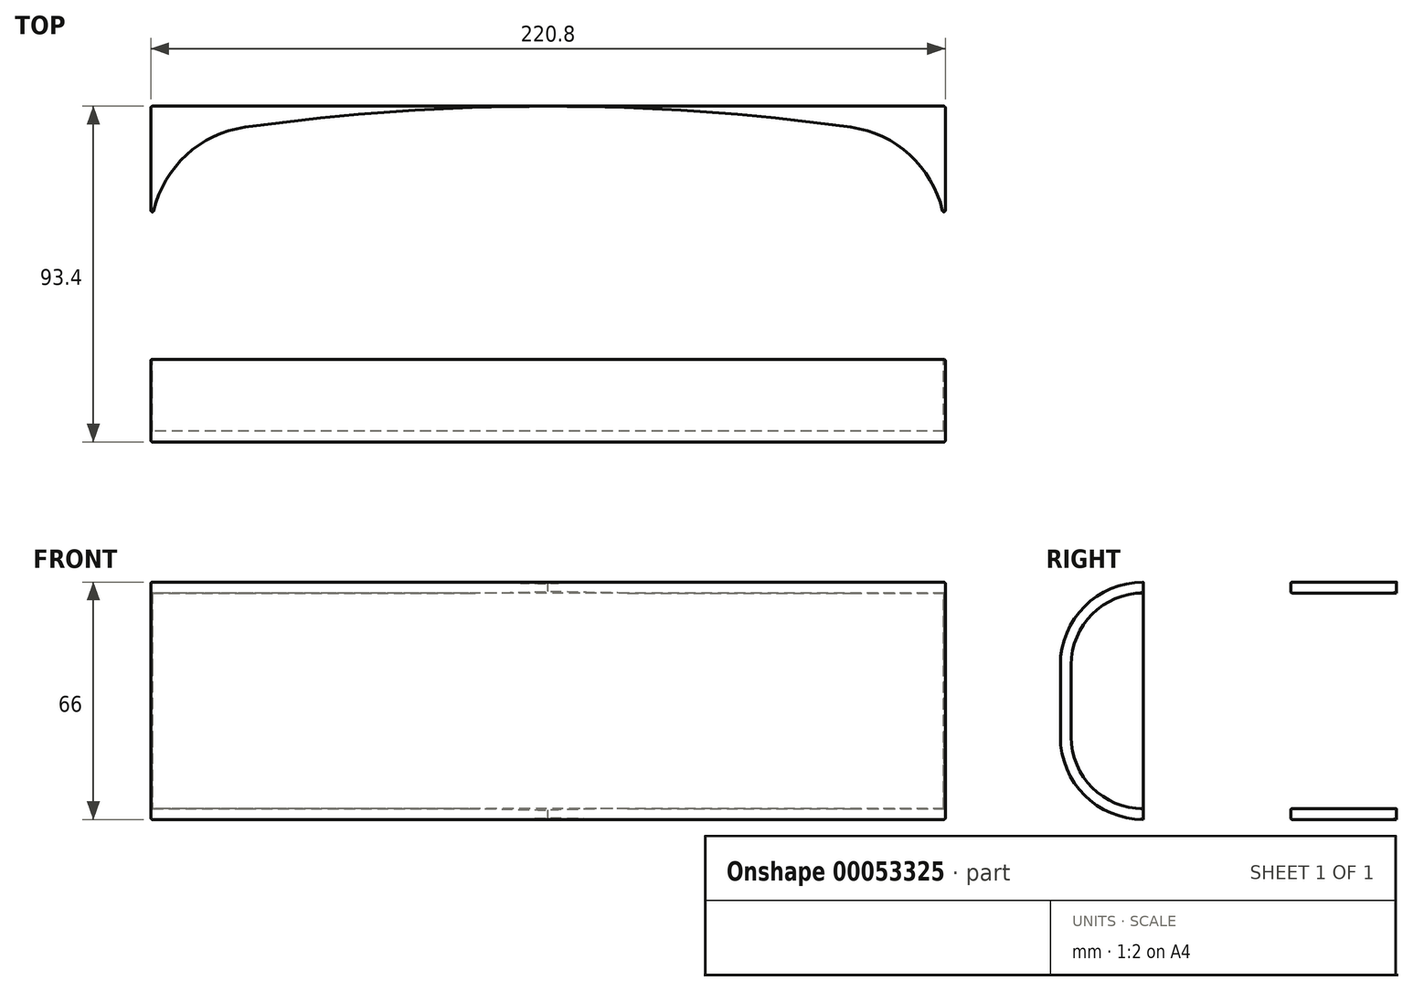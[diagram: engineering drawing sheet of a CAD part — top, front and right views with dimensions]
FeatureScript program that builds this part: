
annotation { "Feature Type Name" : "Feature", "Feature Type Description" : "" }
export const myFeature = defineFeature(function(context is Context, id is Id, definition is map)
    precondition{}
    {
        {
            var Q0;
            Q0=qCreatedBy(makeId("Top.planeOp"),FACE);
            var sketch = newSketch(context, id + "F0", { "sketchPlane" : qUnion([Q0])});
            skLineSegment(sketch, "E0.rect.bottom", {"start": v(110, 40) * mm, "end": v(-110, 40) * mm});
            skLineSegment(sketch, "E0.rect.top", {"start": v(110, -40) * mm, "end": v(-110, -40) * mm});
            skLineSegment(sketch, "E0.rect.left", {"start": v(110, 40) * mm, "end": v(110, -40) * mm});
            skLineSegment(sketch, "E0.rect.right", {"start": v(-110, 40) * mm, "end": v(-110, -40) * mm});
            skPoint(sketch, "E0.rect.middle", {"position": v(0, 0) * mm});
            skArc(sketch, "E1", {"start": v(110, 40) * mm, "mid": v(0, 50) * mm, "end": v(-110, 40) * mm});
            skSolve(sketch);
        }
        {
            var Q0;
            Q0=makeQuery(id+"F0.imprint","IMPRINT",FACE,{"disambiguationData":[TD([[makeQuery(id+"F0.imprint","IMPRINT",EDGE,{"derivedFrom":sQuery(id+"F0.wireOp",EDGE,"E0.rect.bottom")}),1.0]])]});
            var Q1;
            Q1=makeQuery(id+"F0.imprint","IMPRINT",FACE,{"disambiguationData":[TD([[makeQuery(id+"F0.imprint","IMPRINT",EDGE,{"derivedFrom":sQuery(id+"F0.wireOp",EDGE,"E0.rect.bottom")}),-1.0]])]});
            extrude(context, id + "F1", {"entities" : qUnion([Q0, Q1]), "depth" : 60 * mm});
        }
        {
            var Q0;
            Q0=makeQuery(id+"F1.opExtrude","SWEPT_EDGE",EDGE,{"disambiguationData":[OSD([sQuery(id+"F0.wireOp",EDGE,"E0.rect.bottom"),sQuery(id+"F0.wireOp",EDGE,"E0.rect.right"),sQuery(id+"F0.wireOp",EDGE,"E1")])]});
            var Q1;
            Q1=makeQuery(id+"F1.opExtrude","SWEPT_EDGE",EDGE,{"disambiguationData":[OSD([sQuery(id+"F0.wireOp",EDGE,"E0.rect.bottom"),sQuery(id+"F0.wireOp",EDGE,"E0.rect.left"),sQuery(id+"F0.wireOp",EDGE,"E1")])]});
            fillet(context, id + "F2", {"entities" : qUnion([Q0, Q1]), "radius" : 30 * mm, "tangentPropagation" : true, "allowEdgeOverflow" : false});
        }
        {
            var Q0;
            Q0=makeQuery(id+"F1.opExtrude","CAP_EDGE",EDGE,{"disambiguationData":[OSD([sQuery(id+"F0.wireOp",EDGE,"E0.rect.top")])],"isStart":false});
            var Q1;
            Q1=makeQuery(id+"F1.opExtrude","CAP_EDGE",EDGE,{"disambiguationData":[OSD([sQuery(id+"F0.wireOp",EDGE,"E0.rect.top")])],"isStart":true});
            fillet(context, id + "F3", {"entities" : qUnion([Q0, Q1]), "radius" : 20 * mm, "tangentPropagation" : true, "allowEdgeOverflow" : false});
        }
        {
            var Q0;
            Q0=makeQuery(id+"F1.opExtrude","SWEPT_FACE",FACE,{"disambiguationData":[OSD([sQuery(id+"F0.wireOp",EDGE,"E0.rect.left")])]});
            var sketch = newSketch(context, id + "F4", { "sketchPlane" : qUnion([Q0])});
            skLineSegment(sketch, "E2.0", {"start": v(14.46, -3) * mm, "end": v(-20, -3) * mm});
            skLineSegment(sketch, "E2.1", {"start": v(14.46, 63) * mm, "end": v(-20, 63) * mm});
            skArc(sketch, "E2.2", {"start": v(-20, 63) * mm, "mid": v(-36.26, 56.26) * mm, "end": v(-43, 40) * mm});
            skLineSegment(sketch, "E2.3", {"start": v(-43, 40) * mm, "end": v(-43, 20) * mm});
            skArc(sketch, "E2.4", {"start": v(-43, 20) * mm, "mid": v(-36.26, 3.74) * mm, "end": v(-20, -3) * mm});
            skLineSegment(sketch, "E3", {"start": v(14.46, 63) * mm, "end": v(50.4, 63) * mm});
            skLineSegment(sketch, "E4.0.0", {"start": v(50, 60) * mm, "end": v(44.17, 60) * mm});
            skLineSegment(sketch, "E4.0.1", {"start": v(44.17, 60) * mm, "end": v(44.17, 0) * mm});
            skLineSegment(sketch, "E4.0.2", {"start": v(44.17, 0) * mm, "end": v(50, 0) * mm});
            skLineSegment(sketch, "E4.0.3", {"start": v(44.17, 0) * mm, "end": v(44.17, 60) * mm});
            skLineSegment(sketch, "E5", {"start": v(14.46, -3) * mm, "end": v(50.4, -3) * mm});
            skLineSegment(sketch, "E6", {"start": v(50.4, -3) * mm, "end": v(50.4, 0) * mm});
            skLineSegment(sketch, "E7", {"start": v(50.4, 0) * mm, "end": v(50, 0) * mm});
            skLineSegment(sketch, "E8", {"start": v(50, 60) * mm, "end": v(50.4, 60) * mm});
            skLineSegment(sketch, "E9", {"start": v(50.4, 60) * mm, "end": v(50.4, 63) * mm});
            skLineSegment(sketch, "E10.0", {"start": v(14.46, 60) * mm, "end": v(44.17, 60) * mm});
            skLineSegment(sketch, "E11.0", {"start": v(14.46, 60) * mm, "end": v(-20, 60) * mm});
            skArc(sketch, "E12.0", {"start": v(-20, 60) * mm, "mid": v(-34.14, 54.14) * mm, "end": v(-40, 40) * mm});
            skLineSegment(sketch, "E13.0", {"start": v(-40, 40) * mm, "end": v(-40, 20) * mm});
            skArc(sketch, "E14.0", {"start": v(-40, 20) * mm, "mid": v(-34.14, 5.86) * mm, "end": v(-20, 0) * mm});
            skLineSegment(sketch, "E15.0", {"start": v(14.46, 0) * mm, "end": v(-20, 0) * mm});
            skLineSegment(sketch, "E16.0", {"start": v(44.17, 0) * mm, "end": v(14.46, 0) * mm});
            skSolve(sketch);
        }
        {
            var Q0;
            Q0=makeQuery(id+"F4.imprint","IMPRINT",FACE,{"disambiguationData":[TD([[makeQuery(id+"F4.imprint","IMPRINT",EDGE,{"derivedFrom":sQuery(id+"F4.wireOp",EDGE,"E2.0")}),-1.0]])]});
            extrude(context, id + "F5", {"entities" : qUnion([Q0]), "depth" : 0.4 * mm});
        }
        {
            var Q0;
            Q0=makeQuery(id+"F5.opExtrude","CAP_FACE",FACE,{"disambiguationData":[OSD([sQuery(id+"F4.wireOp",EDGE,"E2.0"),sQuery(id+"F4.wireOp",EDGE,"E2.1"),sQuery(id+"F4.wireOp",EDGE,"E2.2"),sQuery(id+"F4.wireOp",EDGE,"E2.3"),sQuery(id+"F4.wireOp",EDGE,"E2.4"),sQuery(id+"F4.wireOp",EDGE,"E3"),sQuery(id+"F4.wireOp",EDGE,"E4.0.0"),sQuery(id+"F4.wireOp",EDGE,"E4.0.2"),sQuery(id+"F4.wireOp",EDGE,"E5"),sQuery(id+"F4.wireOp",EDGE,"E6"),sQuery(id+"F4.wireOp",EDGE,"E7"),sQuery(id+"F4.wireOp",EDGE,"E8"),sQuery(id+"F4.wireOp",EDGE,"E9"),sQuery(id+"F4.wireOp",EDGE,"E10.0"),sQuery(id+"F4.wireOp",EDGE,"E11.0"),sQuery(id+"F4.wireOp",EDGE,"E12.0"),sQuery(id+"F4.wireOp",EDGE,"E13.0"),sQuery(id+"F4.wireOp",EDGE,"E14.0"),sQuery(id+"F4.wireOp",EDGE,"E15.0"),sQuery(id+"F4.wireOp",EDGE,"E16.0")])],"isStart":true});
            extrude(context, id + "F6", {"entities" : qUnion([Q0]), "depth" : 220.4 * mm});
        }
        {
            var Q0;
            Q0=makeQuery(id+"F5.opExtrude","SWEPT_BODY",BODY,{"disambiguationData":[OSD([sQuery(id+"F4.wireOp",EDGE,"E2.0"),sQuery(id+"F4.wireOp",EDGE,"E2.1"),sQuery(id+"F4.wireOp",EDGE,"E2.2"),sQuery(id+"F4.wireOp",EDGE,"E2.3"),sQuery(id+"F4.wireOp",EDGE,"E2.4"),sQuery(id+"F4.wireOp",EDGE,"E3"),sQuery(id+"F4.wireOp",EDGE,"E4.0.0"),sQuery(id+"F4.wireOp",EDGE,"E4.0.2"),sQuery(id+"F4.wireOp",EDGE,"E5"),sQuery(id+"F4.wireOp",EDGE,"E6"),sQuery(id+"F4.wireOp",EDGE,"E7"),sQuery(id+"F4.wireOp",EDGE,"E8"),sQuery(id+"F4.wireOp",EDGE,"E9"),sQuery(id+"F4.wireOp",EDGE,"E10.0"),sQuery(id+"F4.wireOp",EDGE,"E11.0"),sQuery(id+"F4.wireOp",EDGE,"E12.0"),sQuery(id+"F4.wireOp",EDGE,"E13.0"),sQuery(id+"F4.wireOp",EDGE,"E14.0"),sQuery(id+"F4.wireOp",EDGE,"E15.0"),sQuery(id+"F4.wireOp",EDGE,"E16.0")])]});
            var Q1;
            Q1=makeQuery(id+"F6.opExtrude","SWEPT_BODY",BODY,{"disambiguationData":[OSD([sQuery(id+"F4.wireOp",EDGE,"E2.0"),sQuery(id+"F4.wireOp",EDGE,"E2.1"),sQuery(id+"F4.wireOp",EDGE,"E2.2"),sQuery(id+"F4.wireOp",EDGE,"E2.3"),sQuery(id+"F4.wireOp",EDGE,"E2.4"),sQuery(id+"F4.wireOp",EDGE,"E3"),sQuery(id+"F4.wireOp",EDGE,"E4.0.0"),sQuery(id+"F4.wireOp",EDGE,"E4.0.2"),sQuery(id+"F4.wireOp",EDGE,"E5"),sQuery(id+"F4.wireOp",EDGE,"E6"),sQuery(id+"F4.wireOp",EDGE,"E7"),sQuery(id+"F4.wireOp",EDGE,"E8"),sQuery(id+"F4.wireOp",EDGE,"E9"),sQuery(id+"F4.wireOp",EDGE,"E10.0"),sQuery(id+"F4.wireOp",EDGE,"E11.0"),sQuery(id+"F4.wireOp",EDGE,"E12.0"),sQuery(id+"F4.wireOp",EDGE,"E13.0"),sQuery(id+"F4.wireOp",EDGE,"E14.0"),sQuery(id+"F4.wireOp",EDGE,"E15.0"),sQuery(id+"F4.wireOp",EDGE,"E16.0")])]});
            booleanBodies(context, id + "F7", {"operationType" : BooleanOperationType.UNION, "tools" : qUnion([Q0, Q1])});
        }
        {
            var Q0;
            {var subQ0=sQuery(id+"F4.wireOp",EDGE,"E3");var subQ1=sQuery(id+"F4.wireOp",EDGE,"E2.1");Q0=makeQuery(id+"F7.opBoolean","MERGE",FACE,{"derivedFrom":[makeQuery(id+"F5.opExtrude","SWEPT_FACE",FACE,{"disambiguationData":[OSD([subQ1,subQ0])]}),makeQuery(id+"F6.opExtrude","SWEPT_FACE",FACE,{"disambiguationData":[OSD([subQ1,subQ0])]})]});}
            var sketch = newSketch(context, id + "F8", { "sketchPlane" : qUnion([Q0])});
            skArc(sketch, "E17.0", {"start": v(-110, 14.46) * mm, "mid": v(-102.63, 34.15) * mm, "end": v(-84.14, 44.17) * mm});
            skArc(sketch, "E18.0", {"start": v(84.14, 44.17) * mm, "mid": v(0, 50) * mm, "end": v(-84.14, 44.17) * mm});
            skArc(sketch, "E19.0", {"start": v(84.14, 44.17) * mm, "mid": v(102.63, 34.15) * mm, "end": v(110, 14.46) * mm});
            skArc(sketch, "E20.0", {"start": v(-110.4, 14.46) * mm, "mid": v(-102.93, 34.41) * mm, "end": v(-84.2, 44.57) * mm});
            skArc(sketch, "E20.1", {"start": v(84.2, 44.57) * mm, "mid": v(0, 50.4) * mm, "end": v(-84.2, 44.57) * mm});
            skArc(sketch, "E20.2", {"start": v(84.2, 44.57) * mm, "mid": v(102.93, 34.41) * mm, "end": v(110.4, 14.46) * mm});
            skLineSegment(sketch, "E21", {"start": v(110.4, 14.46) * mm, "end": v(110.4, 50.4) * mm});
            skLineSegment(sketch, "E22", {"start": v(110.4, 50.4) * mm, "end": v(-110.4, 50.4) * mm});
            skLineSegment(sketch, "E23", {"start": v(-110.4, 50.4) * mm, "end": v(-110.4, 14.46) * mm});
            skSolve(sketch);
        }
        {
            var Q0;
            {var subQ0=sQuery(id+"F8.wireOp",EDGE,"E20.0");Q0=makeQuery(id+"F8.imprint","IMPRINT",FACE,{"disambiguationData":[TD([[makeQuery(id+"F8.imprint","IMPRINT",EDGE,{"derivedFrom":subQ0}),1.0]])]});}
            var Q1;
            {var subQ0=sQuery(id+"F8.wireOp",EDGE,"E20.2");Q1=makeQuery(id+"F8.imprint","IMPRINT",FACE,{"disambiguationData":[TD([[makeQuery(id+"F8.imprint","IMPRINT",EDGE,{"derivedFrom":subQ0}),1.0]])]});}
            var Q2;
            {var subQ0=sQuery(id+"F4.wireOp",EDGE,"E5");var subQ1=sQuery(id+"F4.wireOp",EDGE,"E2.0");Q2=makeQuery(id+"F7.opBoolean","MERGE",FACE,{"derivedFrom":[makeQuery(id+"F5.opExtrude","SWEPT_FACE",FACE,{"disambiguationData":[OSD([subQ1,subQ0])]}),makeQuery(id+"F6.opExtrude","SWEPT_FACE",FACE,{"disambiguationData":[OSD([subQ1,subQ0])]})]});}
            extrude(context, id + "F9", {"entities" : qUnion([Q0, Q1]), "operationType" : NewBodyOperationType.REMOVE, "endBound" : BoundingType.UP_TO_SURFACE, "oppositeDirection" : true, "endBoundEntityFace" : qUnion([Q2]), "depth" : 25 * mm});
        }
        {
            var Q0;
            Q0=makeQuery(id+"F5.opExtrude","CAP_FACE",FACE,{"disambiguationData":[OSD([sQuery(id+"F4.wireOp",EDGE,"E2.0"),sQuery(id+"F4.wireOp",EDGE,"E2.1"),sQuery(id+"F4.wireOp",EDGE,"E2.2"),sQuery(id+"F4.wireOp",EDGE,"E2.3"),sQuery(id+"F4.wireOp",EDGE,"E2.4"),sQuery(id+"F4.wireOp",EDGE,"E3"),sQuery(id+"F4.wireOp",EDGE,"E4.0.0"),sQuery(id+"F4.wireOp",EDGE,"E4.0.2"),sQuery(id+"F4.wireOp",EDGE,"E5"),sQuery(id+"F4.wireOp",EDGE,"E6"),sQuery(id+"F4.wireOp",EDGE,"E7"),sQuery(id+"F4.wireOp",EDGE,"E8"),sQuery(id+"F4.wireOp",EDGE,"E9"),sQuery(id+"F4.wireOp",EDGE,"E10.0"),sQuery(id+"F4.wireOp",EDGE,"E11.0"),sQuery(id+"F4.wireOp",EDGE,"E12.0"),sQuery(id+"F4.wireOp",EDGE,"E13.0"),sQuery(id+"F4.wireOp",EDGE,"E14.0"),sQuery(id+"F4.wireOp",EDGE,"E15.0"),sQuery(id+"F4.wireOp",EDGE,"E16.0")])],"isStart":false});
            var Q1;
            Q1=makeQuery(id+"F9.boolean.opBoolean","COPY",FACE,{"disambiguationData":[OD(0.0)],"derivedFrom":makeQuery(id+"F9.opExtrude","SWEPT_FACE",FACE,{"disambiguationData":[OSD([sQuery(id+"F8.wireOp",EDGE,"E20.2")])]})});
            var Q2;
            {var subQ0=sQuery(id+"F8.wireOp",EDGE,"E20.1");Q2=makeQuery(id+"F9.boolean.opBoolean","TWEAK_FACE",FACE,{"disambiguationData":[OD(0.0)],"derivedFrom":[makeQuery(id+"F9.opExtrude","SWEPT_FACE",FACE,{"disambiguationData":[OSD([subQ0]),TDD([makeQuery(id+"F8.imprint","IMPRINT",EDGE,{"disambiguationData":[TD([[makeQuery(id+"F8.imprint","INTERSECT",VERTEX,{"derivedFrom":[subQ0,sQuery(id+"F8.wireOp",EDGE,"E20.2")]}),-1.0]])],"derivedFrom":subQ0})])]}),makeQuery(id+"F9.opExtrude","SWEPT_FACE",FACE,{"disambiguationData":[OSD([subQ0]),TDD([makeQuery(id+"F8.imprint","IMPRINT",EDGE,{"disambiguationData":[TD([[makeQuery(id+"F8.imprint","INTERSECT",VERTEX,{"derivedFrom":[sQuery(id+"F8.wireOp",EDGE,"E20.0"),subQ0]}),1.0]])],"derivedFrom":subQ0})])]})]});}
            var Q3;
            Q3=makeQuery(id+"F9.boolean.opBoolean","COPY",FACE,{"disambiguationData":[OD(1.0)],"derivedFrom":makeQuery(id+"F9.opExtrude","SWEPT_FACE",FACE,{"disambiguationData":[OSD([sQuery(id+"F8.wireOp",EDGE,"E20.2")])]})});
            var Q4;
            {var subQ0=sQuery(id+"F8.wireOp",EDGE,"E20.1");Q4=makeQuery(id+"F9.boolean.opBoolean","TWEAK_FACE",FACE,{"disambiguationData":[OD(1.0)],"derivedFrom":[makeQuery(id+"F9.opExtrude","SWEPT_FACE",FACE,{"disambiguationData":[OSD([subQ0]),TDD([makeQuery(id+"F8.imprint","IMPRINT",EDGE,{"disambiguationData":[TD([[makeQuery(id+"F8.imprint","INTERSECT",VERTEX,{"derivedFrom":[subQ0,sQuery(id+"F8.wireOp",EDGE,"E20.2")]}),-1.0]])],"derivedFrom":subQ0})])]}),makeQuery(id+"F9.opExtrude","SWEPT_FACE",FACE,{"disambiguationData":[OSD([subQ0]),TDD([makeQuery(id+"F8.imprint","IMPRINT",EDGE,{"disambiguationData":[TD([[makeQuery(id+"F8.imprint","INTERSECT",VERTEX,{"derivedFrom":[sQuery(id+"F8.wireOp",EDGE,"E20.0"),subQ0]}),1.0]])],"derivedFrom":subQ0})])]})]});}
            var Q5;
            Q5=makeQuery(id+"F9.boolean.opBoolean","COPY",FACE,{"disambiguationData":[OD(0.0)],"derivedFrom":makeQuery(id+"F9.opExtrude","SWEPT_FACE",FACE,{"disambiguationData":[OSD([sQuery(id+"F8.wireOp",EDGE,"E20.0")])]})});
            var Q6;
            Q6=makeQuery(id+"F9.boolean.opBoolean","COPY",FACE,{"disambiguationData":[OD(1.0)],"derivedFrom":makeQuery(id+"F9.opExtrude","SWEPT_FACE",FACE,{"disambiguationData":[OSD([sQuery(id+"F8.wireOp",EDGE,"E20.0")])]})});
            var Q7;
            Q7=makeQuery(id+"F6.opExtrude","CAP_FACE",FACE,{"disambiguationData":[OSD([sQuery(id+"F4.wireOp",EDGE,"E2.0"),sQuery(id+"F4.wireOp",EDGE,"E2.1"),sQuery(id+"F4.wireOp",EDGE,"E2.2"),sQuery(id+"F4.wireOp",EDGE,"E2.3"),sQuery(id+"F4.wireOp",EDGE,"E2.4"),sQuery(id+"F4.wireOp",EDGE,"E3"),sQuery(id+"F4.wireOp",EDGE,"E4.0.0"),sQuery(id+"F4.wireOp",EDGE,"E4.0.2"),sQuery(id+"F4.wireOp",EDGE,"E5"),sQuery(id+"F4.wireOp",EDGE,"E6"),sQuery(id+"F4.wireOp",EDGE,"E7"),sQuery(id+"F4.wireOp",EDGE,"E8"),sQuery(id+"F4.wireOp",EDGE,"E9"),sQuery(id+"F4.wireOp",EDGE,"E10.0"),sQuery(id+"F4.wireOp",EDGE,"E11.0"),sQuery(id+"F4.wireOp",EDGE,"E12.0"),sQuery(id+"F4.wireOp",EDGE,"E13.0"),sQuery(id+"F4.wireOp",EDGE,"E14.0"),sQuery(id+"F4.wireOp",EDGE,"E15.0"),sQuery(id+"F4.wireOp",EDGE,"E16.0")])],"isStart":false});
            fillet(context, id + "F10", {"entities" : qUnion([Q0, Q1, Q2, Q3, Q4, Q5, Q6, Q7]), "radius" : 0.4 * mm, "tangentPropagation" : true, "allowEdgeOverflow" : false});
        }
    });
